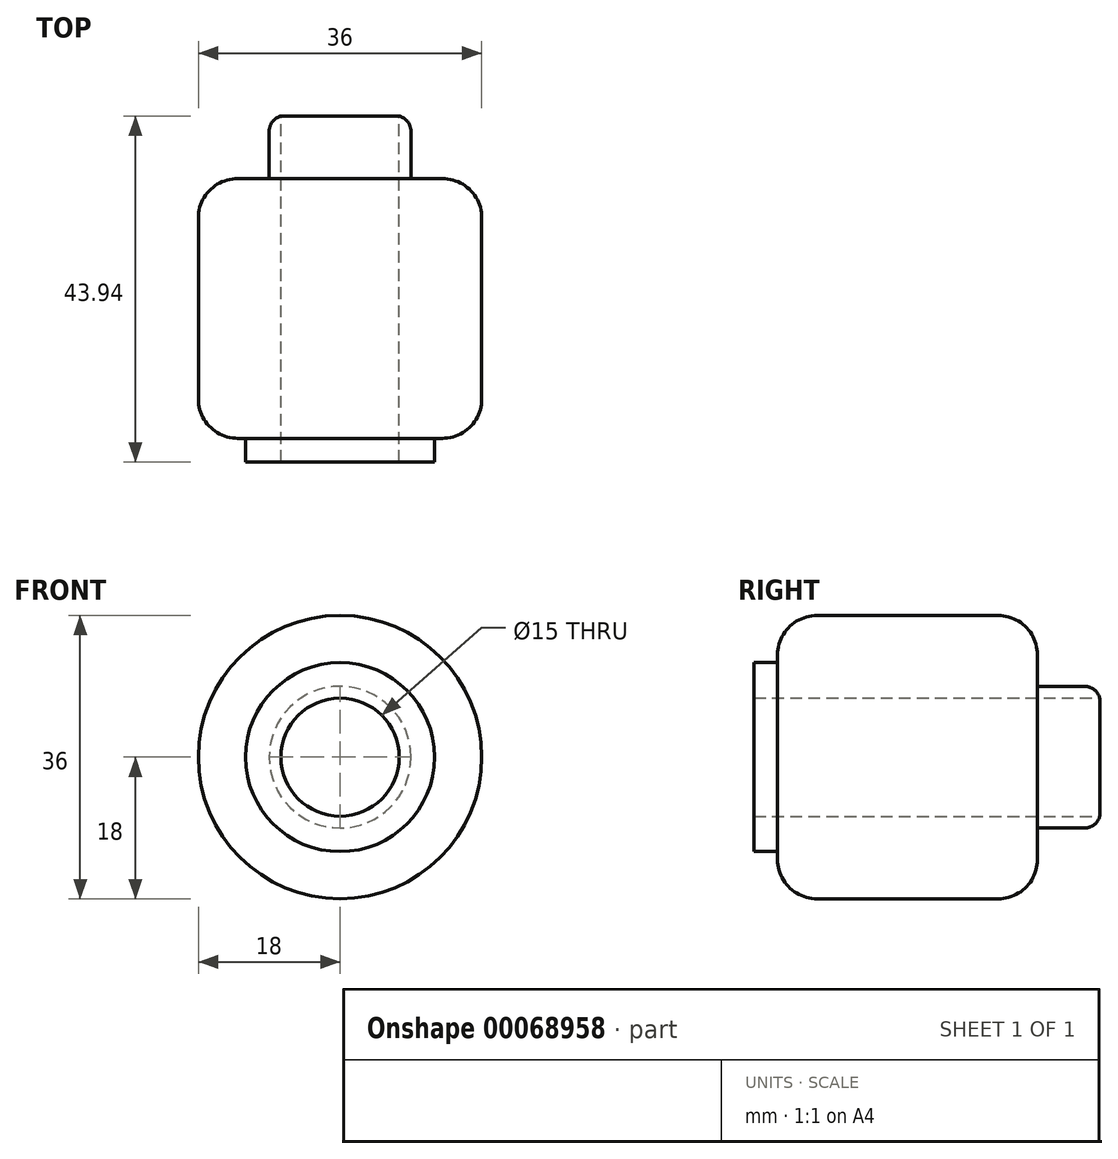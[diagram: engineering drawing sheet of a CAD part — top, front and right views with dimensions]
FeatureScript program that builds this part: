
annotation { "Feature Type Name" : "Feature", "Feature Type Description" : "" }
export const myFeature = defineFeature(function(context is Context, id is Id, definition is map)
    precondition{}
    {
        {
            var Q0;
            Q0=qCreatedBy(makeId("Top.planeOp"),FACE);
            var sketch = newSketch(context, id + "F0", { "sketchPlane" : qUnion([Q0])});
            skLineSegment(sketch, "E0", {"start": v(0, 0) * mm, "end": v(0, 44) * mm});
            skLineSegment(sketch, "E1", {"start": v(0, 44) * mm, "end": v(-7, 44) * mm});
            skLineSegment(sketch, "E2", {"start": v(-9, 42) * mm, "end": v(-9, 36) * mm});
            skLineSegment(sketch, "E3", {"start": v(-9, 36) * mm, "end": v(-13, 36) * mm});
            skLineSegment(sketch, "E4", {"start": v(-18, 31) * mm, "end": v(-18, 8) * mm});
            skLineSegment(sketch, "E5", {"start": v(-13, 3) * mm, "end": v(-12, 3) * mm});
            skLineSegment(sketch, "E6", {"start": v(-12, 3) * mm, "end": v(-12, 0) * mm});
            skLineSegment(sketch, "E7", {"start": v(-12, 0) * mm, "end": v(0, 0) * mm});
            skPoint(sketch, "E8.visualSharp", {"position": v(-18, 36) * mm});
            skArc(sketch, "E8.filletArc", {"start": v(-13, 36) * mm, "mid": v(-16.54, 34.54) * mm, "end": v(-18, 31) * mm});
            skPoint(sketch, "E9.visualSharp", {"position": v(-18, 3) * mm});
            skArc(sketch, "E9.filletArc", {"start": v(-18, 8) * mm, "mid": v(-16.54, 4.46) * mm, "end": v(-13, 3) * mm});
            skPoint(sketch, "E10.visualSharp", {"position": v(-9, 44) * mm});
            skArc(sketch, "E10.filletArc", {"start": v(-7, 44) * mm, "mid": v(-8.41, 43.41) * mm, "end": v(-9, 42) * mm});
            skSolve(sketch);
        }
        {
            var Q0;
            Q0 = qSketchRegion(id + "F0", true);
            var Q1;
            Q1=sQuery(id+"F0.wireOp",EDGE,"E0");
            revolve(context, id + "F1", {"entities" : qUnion([Q0]), "axis" : qUnion([Q1]), "revolveType" : RevolveType.FULL});
        }
        {
            var Q0;
            Q0=makeQuery(id+"F1.opRevolve","SWEPT_FACE",FACE,{"disambiguationData":[OSD([sQuery(id+"F0.wireOp",EDGE,"E1")])]});
            var sketch = newSketch(context, id + "F2", { "sketchPlane" : qUnion([Q0])});
            skCircle(sketch, "E11", {"center": v(0, 0) * mm, "radius": 7.5 * mm});
            skSolve(sketch);
        }
        {
            var Q0;
            Q0 = qSketchRegion(id + "F2", true);
            extrude(context, id + "F3", {"entities" : qUnion([Q0]), "operationType" : NewBodyOperationType.REMOVE, "oppositeDirection" : true, "depth" : 56.33 * mm});
        }
    });
